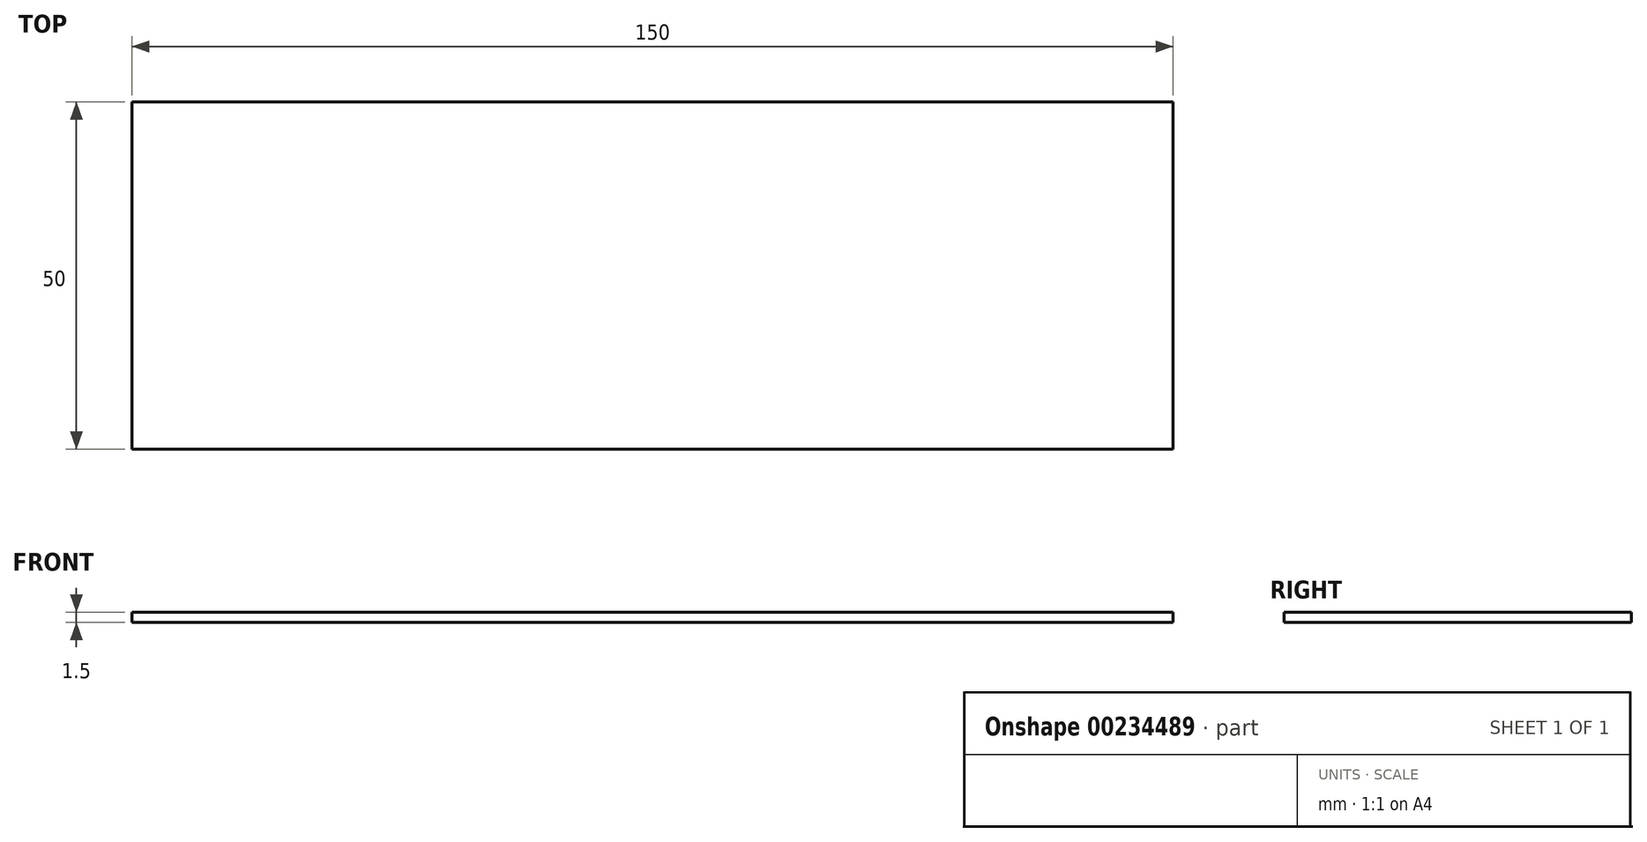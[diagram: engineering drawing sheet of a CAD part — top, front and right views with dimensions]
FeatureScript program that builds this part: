
annotation { "Feature Type Name" : "Feature", "Feature Type Description" : "" }
export const myFeature = defineFeature(function(context is Context, id is Id, definition is map)
    precondition{}
    {
        {
            var Q0;
            Q0=qCreatedBy(makeId("Top.planeOp"),FACE);
            var sketch = newSketch(context, id + "F0", { "sketchPlane" : qUnion([Q0])});
            skLineSegment(sketch, "E0.bottom", {"start": v(-79.1, -11.64) * mm, "end": v(70.9, -11.64) * mm});
            skLineSegment(sketch, "E0.top", {"start": v(-79.1, -61.64) * mm, "end": v(70.9, -61.64) * mm});
            skLineSegment(sketch, "E0.left", {"start": v(-79.1, -11.64) * mm, "end": v(-79.1, -61.64) * mm});
            skLineSegment(sketch, "E0.right", {"start": v(70.9, -11.64) * mm, "end": v(70.9, -61.64) * mm});
            skSolve(sketch);
        }
        {
            var Q0;
            Q0 = qSketchRegion(id + "F0", true);
            extrude(context, id + "F1", {"entities" : qUnion([Q0]), "depth" : 1.5 * mm});
        }
    });
